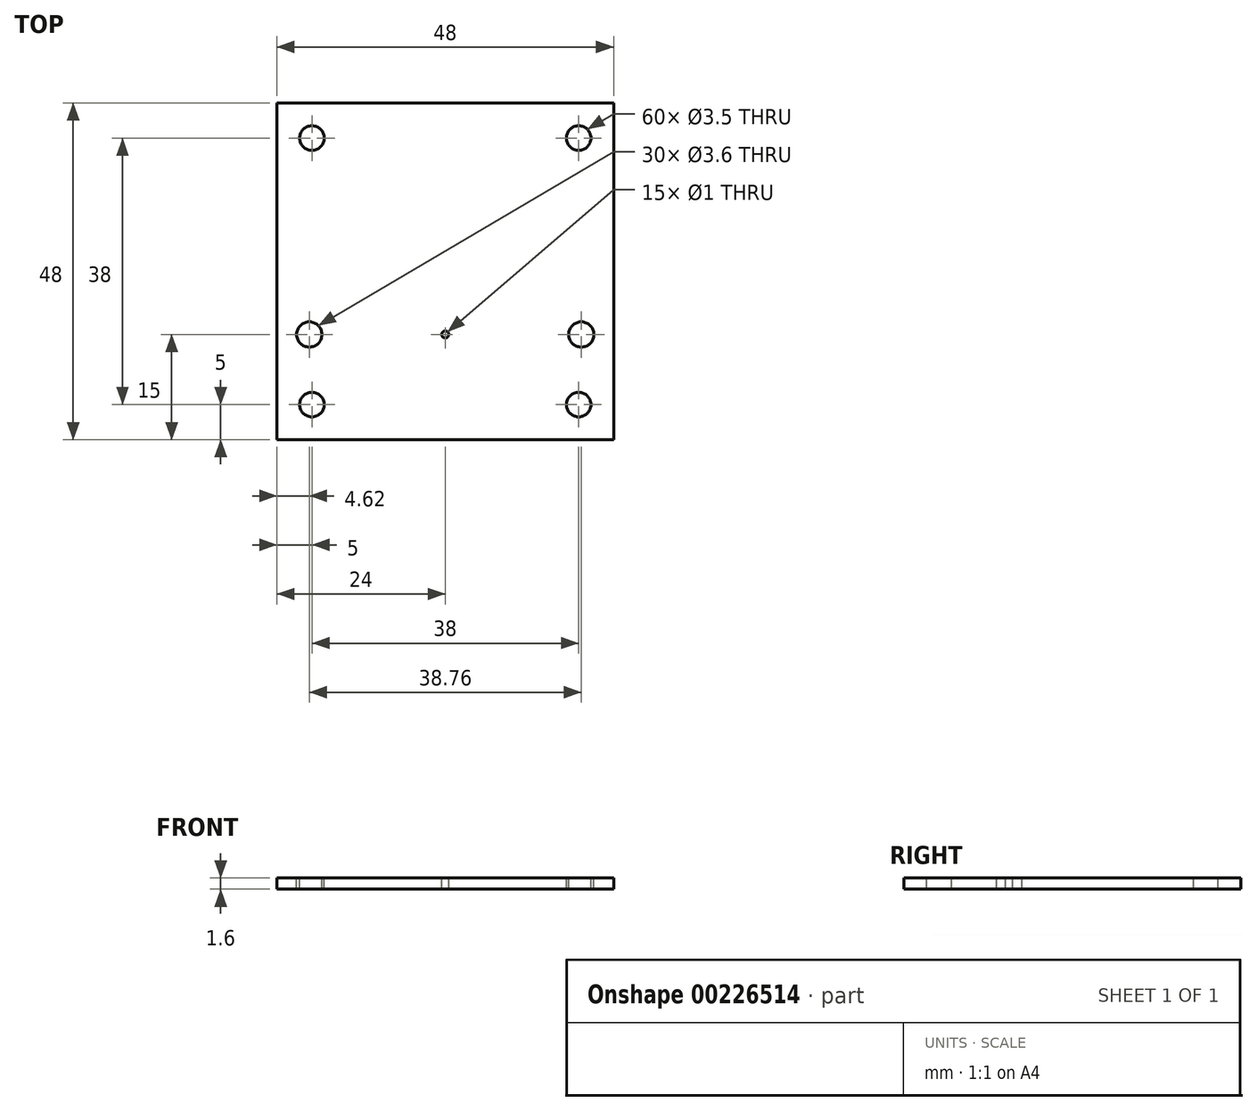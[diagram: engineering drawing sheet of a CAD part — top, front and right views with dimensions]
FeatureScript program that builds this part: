
annotation { "Feature Type Name" : "Feature", "Feature Type Description" : "" }
export const myFeature = defineFeature(function(context is Context, id is Id, definition is map)
    precondition{}
    {
        {
            var Q0;
            Q0=qCreatedBy(makeId("Right.planeOp"),FACE);
            var sketch = newSketch(context, id + "F0", { "sketchPlane" : qUnion([Q0])});
            skLineSegment(sketch, "E0.bottom", {"start": v(24, -0.8) * mm, "end": v(-24, -0.8) * mm});
            skLineSegment(sketch, "E0.top", {"start": v(24, 0.8) * mm, "end": v(-24, 0.8) * mm});
            skLineSegment(sketch, "E0.left", {"start": v(24, -0.8) * mm, "end": v(24, 0.8) * mm});
            skLineSegment(sketch, "E0.right", {"start": v(-24, -0.8) * mm, "end": v(-24, 0.8) * mm});
            skPoint(sketch, "E0.middle", {"position": v(0, 0) * mm});
            skSolve(sketch);
        }
        {
            var Q0;
            Q0=makeQuery(id+"F0.imprint","IMPRINT",FACE,{"disambiguationData":[TD([[makeQuery(id+"F0.imprint","IMPRINT",EDGE,{"derivedFrom":sQuery(id+"F0.wireOp",EDGE,"E0.bottom")}),-1.0]])]});
            extrude(context, id + "F1", {"entities" : qUnion([Q0]), "oppositeDirection" : true, "depth" : 48 * mm});
        }
        {
            var Q0;
            Q0=makeQuery(id+"F1.opExtrude","SWEPT_FACE",FACE,{"disambiguationData":[OSD([sQuery(id+"F0.wireOp",EDGE,"E0.top")])]});
            var sketch = newSketch(context, id + "F2", { "sketchPlane" : qUnion([Q0])});
            skLineSegment(sketch, "E1", {"start": v(-43, -24) * mm, "end": v(-43, 24) * mm, "construction": true});
            skLineSegment(sketch, "E2", {"start": v(-48, -19) * mm, "end": v(0, -19) * mm, "construction": true});
            skPoint(sketch, "E3", {"position": v(-43, -19) * mm});
            skCircle(sketch, "E4", {"center": v(-43, -19) * mm, "radius": 1.75 * mm});
            skLineSegment(sketch, "E5", {"start": v(-48, 19) * mm, "end": v(0, 19) * mm, "construction": true});
            skPoint(sketch, "E6", {"position": v(-43, 19) * mm});
            skCircle(sketch, "E7", {"center": v(-43, 19) * mm, "radius": 1.75 * mm});
            skLineSegment(sketch, "E8", {"start": v(-24, 24) * mm, "end": v(-24, -24) * mm, "construction": true});
            skLineSegment(sketch, "E9", {"start": v(-48, -9) * mm, "end": v(0, -9) * mm, "construction": true});
            skLineSegment(sketch, "E10", {"start": v(-43.38, -6.99) * mm, "end": v(-43.38, -11.87) * mm, "construction": true});
            skLineSegment(sketch, "E11", {"start": v(-4.62, -6.64) * mm, "end": v(-4.62, -12.54) * mm, "construction": true});
            skPoint(sketch, "E12", {"position": v(-24, -9) * mm});
            skCircle(sketch, "E13", {"center": v(-43.38, -9) * mm, "radius": 1.8 * mm});
            skPoint(sketch, "E14", {"position": v(-4.62, -9) * mm});
            skCircle(sketch, "E15", {"center": v(-4.62, -9) * mm, "radius": 1.8 * mm});
            skLineSegment(sketch, "E16", {"start": v(-5, 24) * mm, "end": v(-5, -24) * mm, "construction": true});
            skPoint(sketch, "E17", {"position": v(-5, 19) * mm});
            skPoint(sketch, "E18", {"position": v(-5, -19) * mm});
            skCircle(sketch, "E19", {"center": v(-5, 19) * mm, "radius": 1.75 * mm});
            skCircle(sketch, "E20", {"center": v(-5, -19) * mm, "radius": 1.75 * mm});
            skCircle(sketch, "E21", {"center": v(-24, -9) * mm, "radius": 0.5 * mm});
            skLineSegment(sketch, "E22", {"start": v(-37.3, 24) * mm, "end": v(-37.3, -24) * mm, "construction": true});
            skLineSegment(sketch, "E23", {"start": v(-48, 6.6) * mm, "end": v(0, 6.6) * mm, "construction": true});
            skLineSegment(sketch, "E24", {"start": v(-48, 11.1) * mm, "end": v(0, 11.1) * mm, "construction": true});
            skPoint(sketch, "E25", {"position": v(-24, 11.1) * mm});
            skSolve(sketch);
        }
        {
            var Q0;
            Q0=qSketchRegion(id+"F2",true);
            extrude(context, id + "F3", {"entities" : qUnion([Q0]), "operationType" : NewBodyOperationType.REMOVE, "endBound" : BoundingType.THROUGH_ALL, "oppositeDirection" : true, "depth" : 25 * mm});
        }
        {
            var Q0;
            Q0=qCreatedBy(makeId("Top.planeOp"),FACE);
            var sketch = newSketch(context, id + "F4", { "sketchPlane" : qUnion([Q0])});
            skLineSegment(sketch, "E26.bottom", {"start": v(24, 24) * mm, "end": v(-24, 24) * mm});
            skLineSegment(sketch, "E26.top", {"start": v(24, -24) * mm, "end": v(-24, -24) * mm});
            skLineSegment(sketch, "E26.left", {"start": v(24, 24) * mm, "end": v(24, -24) * mm});
            skLineSegment(sketch, "E26.right", {"start": v(-24, 24) * mm, "end": v(-24, -24) * mm});
            skPoint(sketch, "E26.middle", {"position": v(0, 0) * mm});
            skCircle(sketch, "E27", {"center": v(-19, 19) * mm, "radius": 1.75 * mm});
            skCircle(sketch, "E28", {"center": v(19, 19) * mm, "radius": 1.75 * mm});
            skCircle(sketch, "E29", {"center": v(-19, -19) * mm, "radius": 1.75 * mm});
            skCircle(sketch, "E30", {"center": v(19, -19) * mm, "radius": 1.75 * mm});
            skLineSegment(sketch, "E31.bottom", {"start": v(10, 19) * mm, "end": v(-10, 19) * mm});
            skLineSegment(sketch, "E31.top", {"start": v(10, 10) * mm, "end": v(-10, 10) * mm});
            skLineSegment(sketch, "E31.left", {"start": v(10, 19) * mm, "end": v(10, 10) * mm});
            skLineSegment(sketch, "E31.right", {"start": v(-10, 19) * mm, "end": v(-10, 10) * mm});
            skPoint(sketch, "E31.middle", {"position": v(0, 14.5) * mm});
            skSolve(sketch);
        }
        {
            var Q0;
            Q0=qSketchRegion(id+"F4",true);
            extrude(context, id + "F5", {"entities" : qUnion([Q0]), "depth" : 5 * mm});
        }
        {
            var Q0;
            Q0=makeQuery(id+"F5.opExtrude","SWEPT_BODY",BODY,{"disambiguationData":[OSD([sQuery(id+"F4.wireOp",EDGE,"E26.bottom"),sQuery(id+"F4.wireOp",EDGE,"E26.top"),sQuery(id+"F4.wireOp",EDGE,"E26.left"),sQuery(id+"F4.wireOp",EDGE,"E26.right"),sQuery(id+"F4.wireOp",EDGE,"E27"),sQuery(id+"F4.wireOp",EDGE,"E28"),sQuery(id+"F4.wireOp",EDGE,"E29"),sQuery(id+"F4.wireOp",EDGE,"E30"),sQuery(id+"F4.wireOp",EDGE,"E31.bottom"),sQuery(id+"F4.wireOp",EDGE,"E31.top"),sQuery(id+"F4.wireOp",EDGE,"E31.left"),sQuery(id+"F4.wireOp",EDGE,"E31.right")])]});
            deleteBodies(context, id + "F6", {"entities" : qUnion([Q0])});
        }
    });
